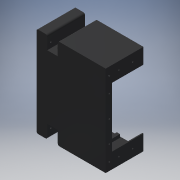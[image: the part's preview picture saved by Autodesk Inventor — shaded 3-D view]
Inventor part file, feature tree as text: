
AUTODESK INVENTOR PART (.ipt)
format: ipt  version: 2016 (Build 200138000, 138)  size: 497,152 bytes
history: native  units: mm
features: extrude x20, sketch x20, fillet x1
ambient origin geometry x8: Origin, YZ Plane, XZ Plane, XY Plane, X Axis, Y Axis, Z Axis, Center Point
bodies: Solid1 (feature_tree)
feature tree (41):
  extrude  "Extrusion1"  Depth=20.0mm
  extrude  "Extrusion2"  Depth=90.0mm
  extrude  "Extrusion3"  Depth=2.0mm
  extrude  "Extrusion4"  Depth=2.0mm
  extrude  "Extrusion5"  Depth=2.0mm
  extrude  "Extrusion6"  Depth=2.0mm
  extrude  "Extrusion7"  Depth=2.0mm
  extrude  "Extrusion8"  Depth=2.0mm
  extrude  "Extrusion9"  Depth=2.0mm
  extrude  "Extrusion10"  Depth=27.0mm
  extrude  "Extrusion11"  Depth=10.0mm TaperAngle=0.0deg
  sketch  "Sketch12"  dims[d27=5.0mm d28=3.0mm]
  extrude  "Extrusion13"  Depth=3.0mm
  extrude  "Extrusion14"  Depth=3.0mm
  extrude  "Extrusion15"  Depth=3.0mm
  extrude  "Extrusion22"  Depth=25.0mm
  extrude  "Extrusion23"  Depth=3.0mm
  extrude  "Extrusion28"  Depth=7.0mm
  extrude  "Extrusion29"  Depth=4.0mm
  fillet  "Fillet1"  Radius=4.0mm
  extrude  "Extrusion30"  Depth=10.0mm
  extrude  "Extrusion31"  Depth=4.0mm TaperAngle=0.0deg
  sketch  "Sketch1"  dims[d0=170.0mm d1=20.0mm]
  sketch  "Sketch2"  dims[d3=20.0mm d4=90.0mm]
  sketch  "Sketch3"  dims[d5=2.0mm d6=0.0mm d7=2.0mm]
  sketch  "Sketch4"  dims[d8=2.0mm d9=2.0mm]
  sketch  "Sketch5"  dims[d10=4.0mm d11=2.0mm]
  sketch  "Sketch6"  dims[d13=2.0mm d14=2.0mm]
  sketch  "Sketch7"  dims[d15=4.0mm d16=2.0mm]
  sketch  "Sketch8"  dims[d17=2.0mm d18=2.0mm]
  sketch  "Sketch9"  dims[d19=2.0mm d20=2.0mm]
  sketch  "Sketch10"  dims[d21=27.0mm d22=27.0mm]
  sketch  "Sketch11"  dims[d23=69.0mm d24=0.0mm d25=10.0mm d26=0.0mm]
  sketch  "Sketch13"  dims[d30=15.0mm d31=3.0mm]
  sketch  "Sketch14"  dims[d32=15.0mm d33=3.0mm]
  sketch  "Sketch22"  dims[d34=20.0mm d35=25.0mm]
  sketch  "Sketch23"  dims[d36=3.0mm d37=3.0mm]
  sketch  "Sketch33"  dims[d38=2.0mm d39=0.0mm d40=7.0mm]
  sketch  "Sketch34"  dims[d41=10.0mm d42=3.2mm d43=4.0mm d44=0.0mm]
  sketch  "Sketch35"  dims[d45=7.0mm d46=10.0mm]
  sketch  "Sketch36"  dims[d47=3.2mm d48=4.0mm d49=0.0mm d50=7.0mm d51=10.0mm d52=3.2mm d53=4.0mm d54=0.0mm d55=7.0mm d56=10.0mm d57=3.2mm d58=4.0mm d59=0.0mm d60=7.0mm d63=3.2mm d64=3.2mm d65=2.0mm d66=0.0mm d67=7.0mm d68=2.625mm d69=3.0mm d70=4.0mm d71=0.0mm d72=7.0mm d73=2.625mm d74=3.0mm d75=4.0mm d76=0.0mm d80=20.0mm d81=150.0mm d82=10.0mm d83=10.0mm d84=90.0mm d85=15.0mm d86=15.0mm d87=14.5mm d88=3.0mm d89=3.0mm d95=6.0mm d96=6.0mm d97=6.0mm d98=6.0mm d99=67.0mm d100=0.0mm d101=67.0mm d102=0.0mm d103=6.0mm d104=3.0mm d105=3.0mm d106=40.0mm d107=0.0mm d167=40.0mm d168=40.0mm d209=11.0mm d210=2.5mm d211=5.0mm d212=5.0mm d213=4.0mm d214=0.0mm d215=11.0mm d216=2.5mm d217=5.0mm d218=5.0mm d219=4.0mm d220=0.0mm d221=3.0mm d222=6.0mm d226=25.0mm d227=25.0mm d228=25.0mm d229=3.0mm d230=3.0mm d231=3.0mm d232=3.0mm d233=3.0mm d292=10.0mm d293=10.0mm d308=3.0mm d309=3.0mm d329=78.0mm d331=4.0mm d332=158.0mm d333=158.0mm d334=78.0mm d335=4.0mm d336=8.0mm d337=8.0mm d338=8.0mm d339=8.0mm d340=8.0mm d341=8.0mm d342=8.0mm d343=8.0mm d344=24.0mm d345=0.0mm d346=15.0mm d347=0.0mm d348=30.4mm d349=2.0mm d350=2.0mm d352=2.0mm d353=2.0mm d354=99.0mm d355=2.0mm d356=34.4mm d357=32.4mm d358=30.4mm d359=28.0mm d360=2.0mm d361=24.0mm d362=0.0mm d364=3.0mm d365=10.0mm d366=10.0mm d367=2.0mm d368=0.0mm d369=10.0mm d370=10.0mm d371=2.0mm d372=0.0mm]
